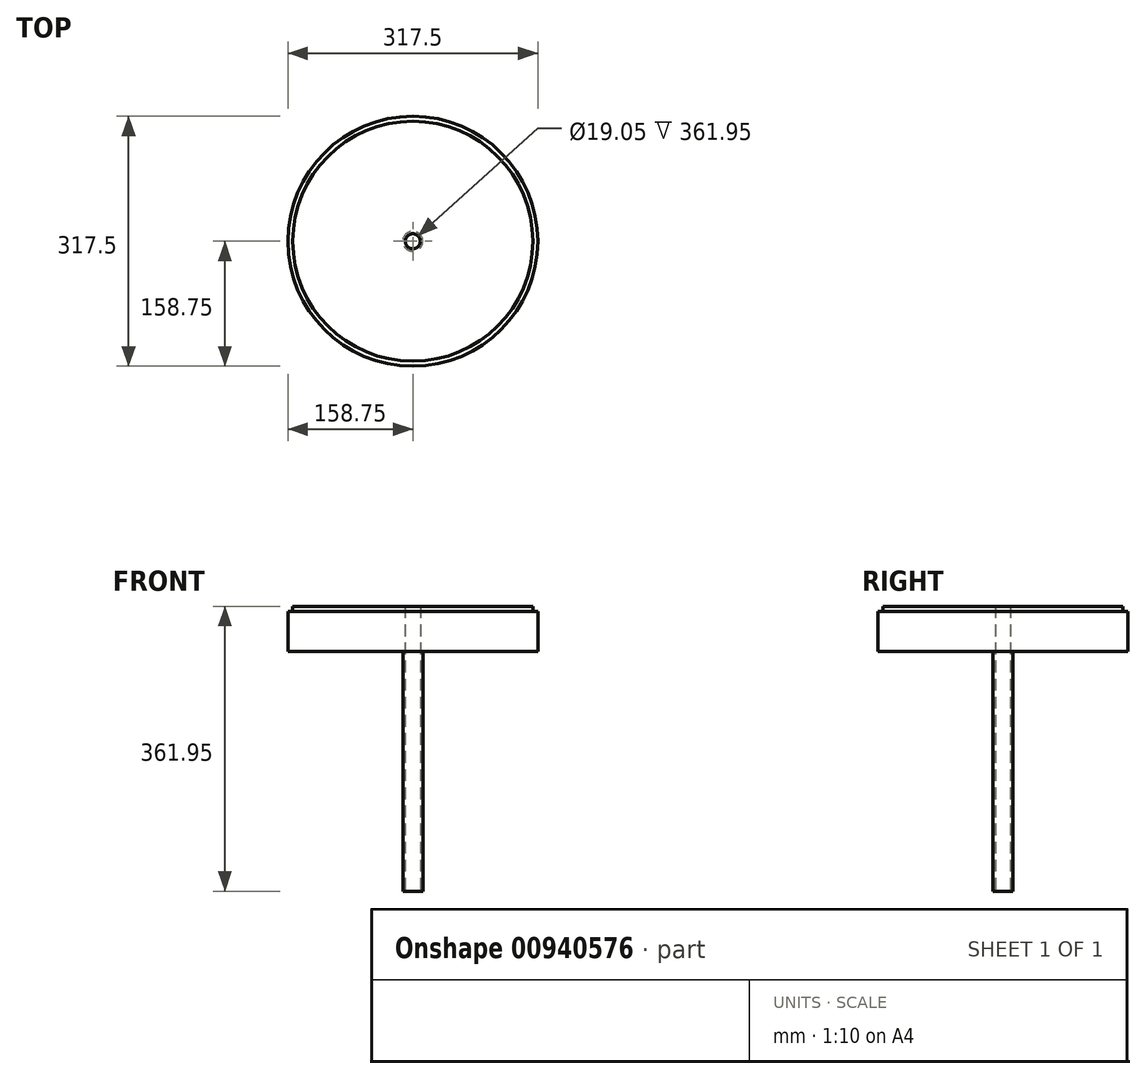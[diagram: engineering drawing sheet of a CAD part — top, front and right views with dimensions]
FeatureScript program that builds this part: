
annotation { "Feature Type Name" : "Feature", "Feature Type Description" : "" }
export const myFeature = defineFeature(function(context is Context, id is Id, definition is map)
    precondition{}
    {
        {
            var Q0;
            Q0=qCreatedBy(makeId("Top.planeOp"),FACE);
            var sketch = newSketch(context, id + "F0", { "sketchPlane" : qUnion([Q0])});
            skCircle(sketch, "E0", {"center": v(0, 0) * mm, "radius": 152.4 * mm});
            skSolve(sketch);
        }
        {
            var Q0;
            Q0=makeQuery(id+"F0.imprint","IMPRINT",FACE,{"disambiguationData":[TD([[makeQuery(id+"F0.imprint","IMPRINT",EDGE,{"derivedFrom":sQuery(id+"F0.wireOp",EDGE,"E0")}),1.0]])]});
            var Q1;
            Q1=sQuery(id+"F0.wireOp",EDGE,"E0");
            extrude(context, id + "F1", {"entities" : qUnion([Q0]), "surfaceEntities" : qUnion([Q1]), "oppositeDirection" : true, "depth" : 6.35 * mm, "offsetDistance" : 25.4 * mm});
        }
        {
            var Q0;
            Q0=makeQuery(id+"F1.opExtrude","CAP_FACE",FACE,{"disambiguationData":[OSD([sQuery(id+"F0.wireOp",EDGE,"E0")])],"isStart":false});
            var sketch = newSketch(context, id + "F2", { "sketchPlane" : qUnion([Q0])});
            skCircle(sketch, "E1", {"center": v(0, 0) * mm, "radius": 158.75 * mm});
            skSolve(sketch);
        }
        {
            var Q0;
            Q0 = qSketchRegion(id + "F2", true);
            extrude(context, id + "F3", {"entities" : qUnion([Q0]), "operationType" : NewBodyOperationType.ADD, "depth" : 50.8 * mm, "offsetDistance" : 25.4 * mm});
        }
        {
            var Q0;
            Q0=makeQuery(id+"F1.opExtrude","CAP_FACE",FACE,{"disambiguationData":[OSD([sQuery(id+"F0.wireOp",EDGE,"E0")])],"isStart":true});
            var sketch = newSketch(context, id + "F4", { "sketchPlane" : qUnion([Q0])});
            skCircle(sketch, "E2", {"center": v(0, 0) * mm, "radius": 6.35 * mm});
            skSolve(sketch);
        }
        {
            var Q0;
            Q0=makeQuery(id+"F4.imprint","IMPRINT",FACE,{"disambiguationData":[TD([[makeQuery(id+"F4.imprint","IMPRINT",EDGE,{"derivedFrom":sQuery(id+"F4.wireOp",EDGE,"E2")}),1.0]])]});
            var Q1;
            Q1=sQuery(id+"F4.wireOp",EDGE,"E2");
            extrude(context, id + "F5", {"entities" : qUnion([Q0]), "operationType" : NewBodyOperationType.REMOVE, "surfaceEntities" : qUnion([Q1]), "endBound" : BoundingType.THROUGH_ALL, "oppositeDirection" : true, "depth" : 25.4 * mm, "offsetDistance" : 25.4 * mm});
        }
        {
            var Q0;
            Q0=makeQuery(id+"F3.opExtrude","CAP_FACE",FACE,{"disambiguationData":[OSD([sQuery(id+"F2.wireOp",EDGE,"E1")])],"isStart":false});
            var sketch = newSketch(context, id + "F6", { "sketchPlane" : qUnion([Q0])});
            skCircle(sketch, "E3", {"center": v(0, 0) * mm, "radius": 12.7 * mm});
            skSolve(sketch);
        }
        {
            var Q0;
            Q0 = qSketchRegion(id + "F6", true);
            extrude(context, id + "F7", {"entities" : qUnion([Q0]), "operationType" : NewBodyOperationType.ADD, "depth" : 304.8 * mm, "offsetDistance" : 25.4 * mm});
        }
        {
            var Q0;
            Q0=makeQuery(id+"F7.opExtrude","CAP_FACE",FACE,{"disambiguationData":[OSD([sQuery(id+"F6.wireOp",EDGE,"E3")])],"isStart":false});
            var sketch = newSketch(context, id + "F8", { "sketchPlane" : qUnion([Q0])});
            skCircle(sketch, "E4", {"center": v(0, 0) * mm, "radius": 9.53 * mm});
            skSolve(sketch);
        }
        {
            var Q0;
            Q0 = qSketchRegion(id + "F8", true);
            extrude(context, id + "F9", {"entities" : qUnion([Q0]), "operationType" : NewBodyOperationType.REMOVE, "endBound" : BoundingType.UP_TO_NEXT, "oppositeDirection" : true, "depth" : 25.4 * mm, "offsetDistance" : 25.4 * mm});
        }
    });
